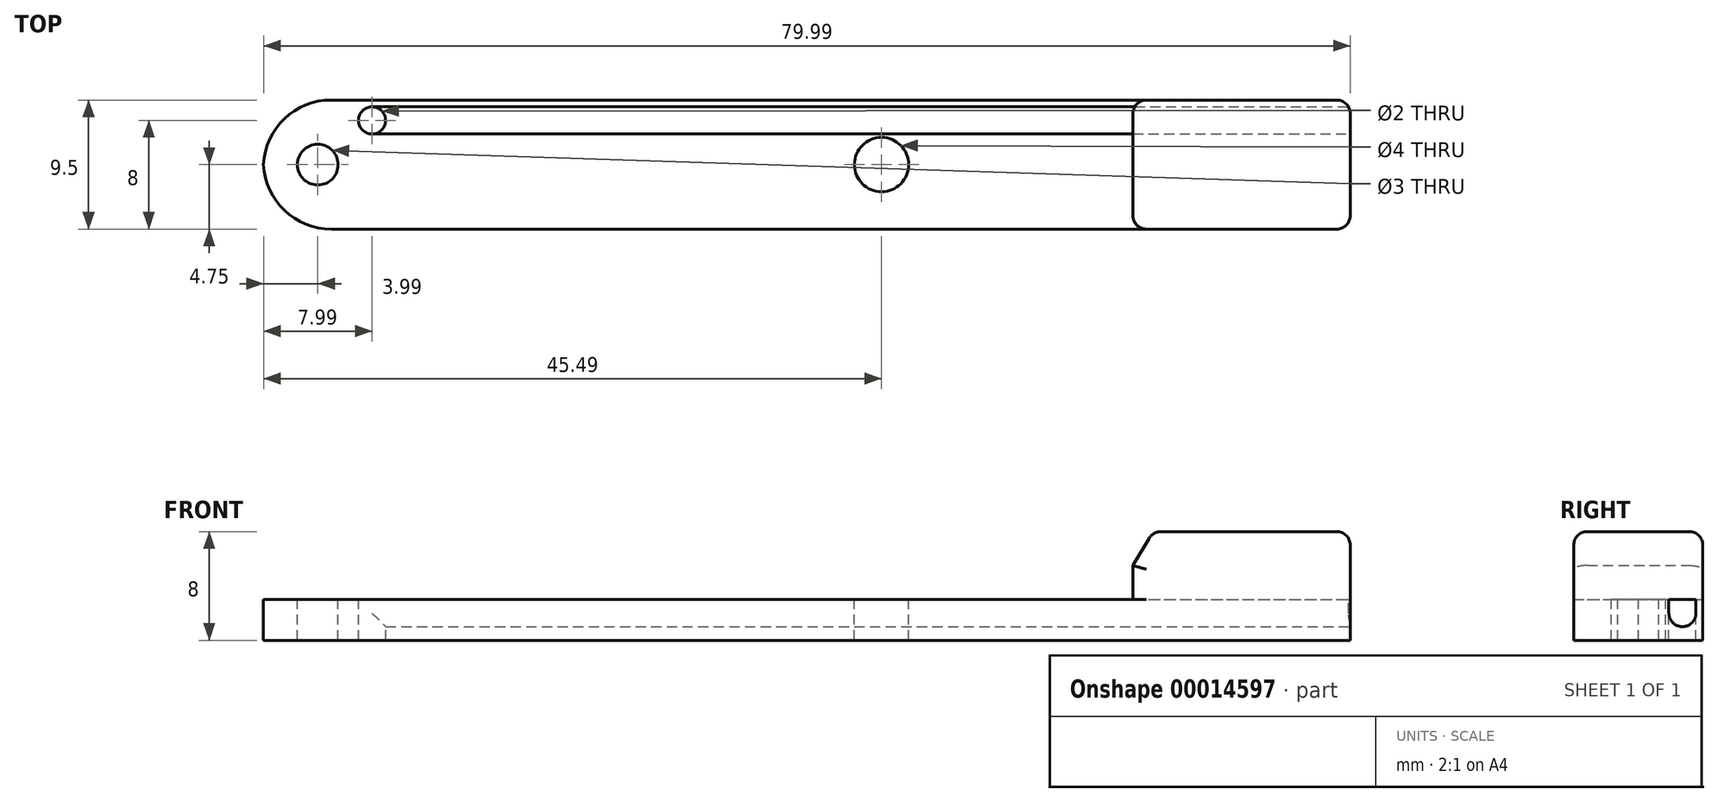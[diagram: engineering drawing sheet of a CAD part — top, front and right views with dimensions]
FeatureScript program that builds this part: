
annotation { "Feature Type Name" : "Feature", "Feature Type Description" : "" }
export const myFeature = defineFeature(function(context is Context, id is Id, definition is map)
    precondition{}
    {
        {
            var Q0;
            Q0=qCreatedBy(makeId("Front.planeOp"),FACE);
            var sketch = newSketch(context, id + "F0", { "sketchPlane" : qUnion([Q0])});
            skLineSegment(sketch, "E0.bottom", {"start": v(0, 0) * mm, "end": v(-80, 0) * mm});
            skLineSegment(sketch, "E0.top", {"start": v(-16, 3) * mm, "end": v(-80, 3) * mm});
            skLineSegment(sketch, "E0.left", {"start": v(0, 0) * mm, "end": v(0, 3) * mm});
            skLineSegment(sketch, "E0.right", {"start": v(-80, 0) * mm, "end": v(-80, 3) * mm});
            skLineSegment(sketch, "E1.top", {"start": v(0, 8) * mm, "end": v(-14.5, 8) * mm});
            skLineSegment(sketch, "E1.left", {"start": v(0, 3) * mm, "end": v(0, 8) * mm});
            skLineSegment(sketch, "E1.right", {"start": v(-16, 3) * mm, "end": v(-16, 5.5) * mm});
            skLineSegment(sketch, "E2", {"start": v(-16, 5.5) * mm, "end": v(-14.5, 8) * mm});
            skPoint(sketch, "E3.orphan", {"position": v(-16, 8) * mm});
            skSolve(sketch);
        }
        {
            var Q0;
            Q0=makeQuery(id+"F0.imprint","IMPRINT",FACE,{"disambiguationData":[TD([[makeQuery(id+"F0.imprint","IMPRINT",EDGE,{"derivedFrom":sQuery(id+"F0.wireOp",EDGE,"E0.bottom")}),-1.0]])]});
            extrude(context, id + "F1", {"entities" : qUnion([Q0]), "depth" : 9.5 * mm});
        }
        {
            var Q0;
            Q0=makeQuery(id+"F1.opExtrude","SWEPT_FACE",FACE,{"disambiguationData":[OSD([sQuery(id+"F0.wireOp",EDGE,"E0.top")])]});
            var sketch = newSketch(context, id + "F2", { "sketchPlane" : qUnion([Q0])});
            skLineSegment(sketch, "E4", {"start": v(-80, -4.75) * mm, "end": v(-16, -4.75) * mm, "construction": true});
            skCircle(sketch, "E5", {"center": v(-76, -4.75) * mm, "radius": 1.5 * mm});
            skCircle(sketch, "E6", {"center": v(-34.5, -4.75) * mm, "radius": 2 * mm});
            skLineSegment(sketch, "E7", {"start": v(-72, -4.75) * mm, "end": v(-72, 0) * mm, "construction": true});
            skCircle(sketch, "E8", {"center": v(-72, -1.5) * mm, "radius": 1 * mm});
            skSolve(sketch);
        }
        {
            var Q0;
            Q0 = qSketchRegion(id + "F2", true);
            extrude(context, id + "F3", {"entities" : qUnion([Q0]), "operationType" : NewBodyOperationType.REMOVE, "endBound" : BoundingType.THROUGH_ALL, "oppositeDirection" : true, "depth" : 25 * mm});
        }
        {
            var Q0;
            Q0=makeQuery(id+"F1.opExtrude","SWEPT_FACE",FACE,{"disambiguationData":[OSD([sQuery(id+"F0.wireOp",EDGE,"E0.left"),sQuery(id+"F0.wireOp",EDGE,"E1.left")])]});
            var sketch = newSketch(context, id + "F4", { "sketchPlane" : qUnion([Q0])});
            skLineSegment(sketch, "E9.0", {"start": v(-9.5, 3) * mm, "end": v(0, 3) * mm, "construction": true});
            skArc(sketch, "E10", {"start": v(-2.5, 2) * mm, "mid": v(-1.5, 1) * mm, "end": v(-0.5, 2) * mm});
            skLineSegment(sketch, "E11.0", {"start": v(-2.5, 3) * mm, "end": v(-0.5, 3) * mm});
            skLineSegment(sketch, "E12", {"start": v(-0.5, 3) * mm, "end": v(-0.5, 2) * mm});
            skLineSegment(sketch, "E13", {"start": v(-2.5, 3) * mm, "end": v(-2.5, 2) * mm});
            skSolve(sketch);
        }
        {
            var Q0;
            Q0=makeQuery(id+"F4.imprint","IMPRINT",FACE,{"disambiguationData":[TD([[makeQuery(id+"F4.imprint","IMPRINT",EDGE,{"derivedFrom":sQuery(id+"F4.wireOp",EDGE,"E10")}),1.0]])]});
            var Q1;
            Q1=makeQuery(id+"F3.boolean.opBoolean","COPY",FACE,{"derivedFrom":makeQuery(id+"F3.opExtrude","SWEPT_FACE",FACE,{"disambiguationData":[OSD([sQuery(id+"F2.wireOp",EDGE,"E8")])]})});
            extrude(context, id + "F5", {"entities" : qUnion([Q0]), "operationType" : NewBodyOperationType.REMOVE, "endBound" : BoundingType.UP_TO_SURFACE, "oppositeDirection" : true, "endBoundEntityFace" : qUnion([Q1]), "depth" : 25 * mm});
        }
        {
            var Q0;
            Q0=makeQuery(id+"F1.opExtrude","CAP_EDGE",EDGE,{"disambiguationData":[OSD([sQuery(id+"F0.wireOp",EDGE,"E0.right")])],"isStart":false});
            var Q1;
            Q1=makeQuery(id+"F1.opExtrude","CAP_EDGE",EDGE,{"disambiguationData":[OSD([sQuery(id+"F0.wireOp",EDGE,"E0.right")])],"isStart":true});
            fillet(context, id + "F6", {"entities" : qUnion([Q0, Q1]), "radius" : 5 * mm, "tangentPropagation" : true, "allowEdgeOverflow" : false});
        }
        {
            var Q0;
            Q0=makeQuery(id+"F1.opExtrude","CAP_EDGE",EDGE,{"disambiguationData":[OSD([sQuery(id+"F0.wireOp",EDGE,"E1.right")])],"isStart":false});
            var Q1;
            Q1=makeQuery(id+"F1.opExtrude","CAP_EDGE",EDGE,{"disambiguationData":[OSD([sQuery(id+"F0.wireOp",EDGE,"E2")])],"isStart":false});
            var Q2;
            Q2=makeQuery(id+"F1.opExtrude","CAP_EDGE",EDGE,{"disambiguationData":[OSD([sQuery(id+"F0.wireOp",EDGE,"E1.top")])],"isStart":false});
            var Q3;
            Q3=makeQuery(id+"F1.opExtrude","SWEPT_EDGE",EDGE,{"disambiguationData":[OSD([sQuery(id+"F0.wireOp",EDGE,"E1.top"),sQuery(id+"F0.wireOp",EDGE,"E1.left")])]});
            var Q4;
            Q4=makeQuery(id+"F1.opExtrude","CAP_EDGE",EDGE,{"disambiguationData":[OSD([sQuery(id+"F0.wireOp",EDGE,"E0.left"),sQuery(id+"F0.wireOp",EDGE,"E1.left")])],"isStart":false});
            var Q5;
            Q5=makeQuery(id+"F1.opExtrude","CAP_EDGE",EDGE,{"disambiguationData":[OSD([sQuery(id+"F0.wireOp",EDGE,"E1.top")])],"isStart":true});
            var Q6;
            Q6=makeQuery(id+"F1.opExtrude","CAP_EDGE",EDGE,{"disambiguationData":[OSD([sQuery(id+"F0.wireOp",EDGE,"E2")])],"isStart":true});
            var Q7;
            Q7=makeQuery(id+"F1.opExtrude","CAP_EDGE",EDGE,{"disambiguationData":[OSD([sQuery(id+"F0.wireOp",EDGE,"E1.right")])],"isStart":true});
            var Q8;
            Q8=makeQuery(id+"F1.opExtrude","SWEPT_EDGE",EDGE,{"disambiguationData":[OSD([sQuery(id+"F0.wireOp",EDGE,"E1.top"),sQuery(id+"F0.wireOp",EDGE,"E2")])]});
            var Q9;
            Q9=makeQuery(id+"F1.opExtrude","CAP_EDGE",EDGE,{"disambiguationData":[OSD([sQuery(id+"F0.wireOp",EDGE,"E0.left"),sQuery(id+"F0.wireOp",EDGE,"E1.left")])],"isStart":true});
            fillet(context, id + "F7", {"entities" : qUnion([Q0, Q1, Q2, Q3, Q4, Q5, Q6, Q7, Q8, Q9]), "radius" : 1 * mm, "tangentPropagation" : true, "allowEdgeOverflow" : false});
        }
    });
